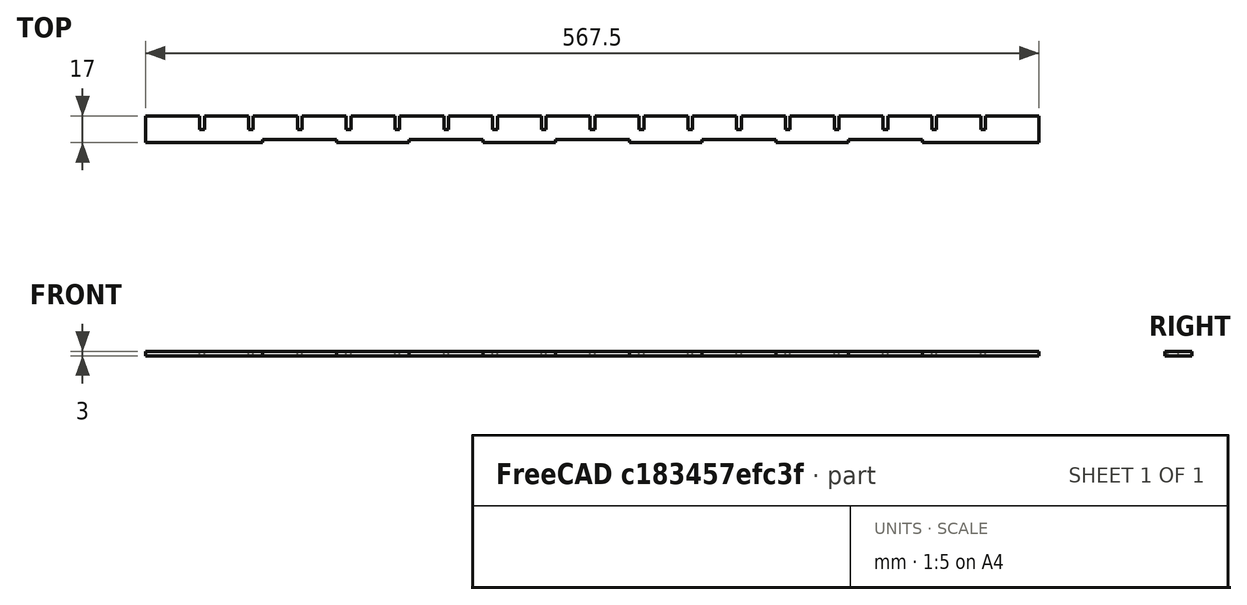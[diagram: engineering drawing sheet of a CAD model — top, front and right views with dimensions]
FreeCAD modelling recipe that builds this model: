
FCSTD DOCUMENT  (FreeCAD 0.16R6706 (Git))
Label: Leiste_lang_mitAufnahme_2x
License: All rights reserved
LicenseURL: http://de.wikipedia.org/wiki/Alle_Rechte_vorbehalten
objects: Sketcher::SketchObject×1, PartDesign::Pad×1
note: 3 computed .brp shape members not serialized (recipe doc carries the construction recipe); baked Part::Feature solids carry a one-line shape summary decoded from their .brp

FEATURE [Sketcher::SketchObject] Sketch
  sketch-geometry (97):
    g0: LineSegment StartX=0 StartY=0 StartZ=0 EndX=0 EndY=17 EndZ=0
    g1: LineSegment StartX=0 StartY=17 StartZ=0 EndX=34.5 EndY=17 EndZ=0
    g2: LineSegment StartX=34.5 StartY=17 StartZ=0 EndX=34.5 EndY=8.5 EndZ=0
    g3: LineSegment StartX=34.5 StartY=8.5 StartZ=0 EndX=37.5 EndY=8.5 EndZ=0
    g4: LineSegment StartX=37.5 StartY=8.5 StartZ=0 EndX=37.5 EndY=17 EndZ=0
    g5: LineSegment StartX=37.5 StartY=17 StartZ=0 EndX=65.5 EndY=17 EndZ=0
    g6: LineSegment StartX=65.5 StartY=17 StartZ=0 EndX=65.5 EndY=8.5 EndZ=0
    g7: LineSegment StartX=65.5 StartY=8.5 StartZ=0 EndX=68.5 EndY=8.5 EndZ=0
    g8: LineSegment StartX=68.5 StartY=8.5 StartZ=0 EndX=68.5 EndY=17 EndZ=0
    g9: LineSegment StartX=68.5 StartY=17 StartZ=0 EndX=96.5 EndY=17 EndZ=0
    g10: LineSegment StartX=96.5 StartY=17 StartZ=0 EndX=96.5 EndY=8.5 EndZ=0
    g11: LineSegment StartX=96.5 StartY=8.5 StartZ=0 EndX=99.5 EndY=8.5 EndZ=0
    g12: LineSegment StartX=99.5 StartY=8.5 StartZ=0 EndX=99.5 EndY=17 EndZ=0
    g13: LineSegment StartX=99.5 StartY=17 StartZ=0 EndX=127.5 EndY=17 EndZ=0
    g14: LineSegment StartX=127.5 StartY=17 StartZ=0 EndX=127.5 EndY=8.5 EndZ=0
    g15: LineSegment StartX=127.5 StartY=8.5 StartZ=0 EndX=130.5 EndY=8.5 EndZ=0
    g16: LineSegment StartX=130.5 StartY=8.5 StartZ=0 EndX=130.5 EndY=17 EndZ=0
    g17: LineSegment StartX=130.5 StartY=17 StartZ=0 EndX=158.5 EndY=17 EndZ=0
    g18: LineSegment StartX=158.5 StartY=17 StartZ=0 EndX=158.5 EndY=8.5 EndZ=0
    g19: LineSegment StartX=158.5 StartY=8.5 StartZ=0 EndX=161.5 EndY=8.5 EndZ=0
    g20: LineSegment StartX=161.5 StartY=8.5 StartZ=0 EndX=161.5 EndY=17 EndZ=0
    g21: LineSegment StartX=161.5 StartY=17 StartZ=0 EndX=189.5 EndY=17 EndZ=0
    g22: LineSegment StartX=189.5 StartY=17 StartZ=0 EndX=189.5 EndY=8.5 EndZ=0
    g23: LineSegment StartX=189.5 StartY=8.5 StartZ=0 EndX=192.5 EndY=8.5 EndZ=0
    g24: LineSegment StartX=192.5 StartY=8.5 StartZ=0 EndX=192.5 EndY=17 EndZ=0
    g25: LineSegment StartX=192.5 StartY=17 StartZ=0 EndX=220.5 EndY=17 EndZ=0
    g26: LineSegment StartX=220.5 StartY=17 StartZ=0 EndX=220.5 EndY=8.5 EndZ=0
    g27: LineSegment StartX=220.5 StartY=8.5 StartZ=0 EndX=223.5 EndY=8.5 EndZ=0
    g28: LineSegment StartX=223.5 StartY=8.5 StartZ=0 EndX=223.5 EndY=17 EndZ=0
    g29: LineSegment StartX=223.5 StartY=17 StartZ=0 EndX=251.5 EndY=17 EndZ=0
    g30: LineSegment StartX=251.5 StartY=17 StartZ=0 EndX=251.5 EndY=8.5 EndZ=0
    g31: LineSegment StartX=251.5 StartY=8.5 StartZ=0 EndX=254.5 EndY=8.5 EndZ=0
    g32: LineSegment StartX=254.5 StartY=8.5 StartZ=0 EndX=254.5 EndY=17 EndZ=0
    g33: LineSegment StartX=254.5 StartY=17 StartZ=0 EndX=282.5 EndY=17 EndZ=0
    g34: LineSegment StartX=282.5 StartY=17 StartZ=0 EndX=282.5 EndY=8.5 EndZ=0
    g35: LineSegment StartX=282.5 StartY=8.5 StartZ=0 EndX=285.5 EndY=8.5 EndZ=0
    g36: LineSegment StartX=285.5 StartY=8.5 StartZ=0 EndX=285.5 EndY=17 EndZ=0
    g37: LineSegment StartX=285.5 StartY=17 StartZ=0 EndX=313.5 EndY=17 EndZ=0
    g38: LineSegment StartX=313.5 StartY=17 StartZ=0 EndX=313.5 EndY=8.5 EndZ=0
    g39: LineSegment StartX=313.5 StartY=8.5 StartZ=0 EndX=316.5 EndY=8.5 EndZ=0
    g40: LineSegment StartX=316.5 StartY=8.5 StartZ=0 EndX=316.5 EndY=17 EndZ=0
    g41: LineSegment StartX=316.5 StartY=17 StartZ=0 EndX=344.5 EndY=17 EndZ=0
    g42: LineSegment StartX=344.5 StartY=17 StartZ=0 EndX=344.5 EndY=8.5 EndZ=0
    g43: LineSegment StartX=344.5 StartY=8.5 StartZ=0 EndX=347.5 EndY=8.5 EndZ=0
    g44: LineSegment StartX=347.5 StartY=8.5 StartZ=0 EndX=347.5 EndY=17 EndZ=0
    g45: LineSegment StartX=347.5 StartY=17 StartZ=0 EndX=375.5 EndY=17 EndZ=0
    g46: LineSegment StartX=375.5 StartY=17 StartZ=0 EndX=375.5 EndY=8.5 EndZ=0
    g47: LineSegment StartX=375.5 StartY=8.5 StartZ=0 EndX=378.5 EndY=8.5 EndZ=0
    g48: LineSegment StartX=378.5 StartY=8.5 StartZ=0 EndX=378.5 EndY=17 EndZ=0
    g49: LineSegment StartX=378.5 StartY=17 StartZ=0 EndX=406.5 EndY=17 EndZ=0
    g50: LineSegment StartX=406.5 StartY=17 StartZ=0 EndX=406.5 EndY=8.5 EndZ=0
    g51: LineSegment StartX=406.5 StartY=8.5 StartZ=0 EndX=409.5 EndY=8.5 EndZ=0
    g52: LineSegment StartX=409.5 StartY=8.5 StartZ=0 EndX=409.5 EndY=17 EndZ=0
    g53: LineSegment StartX=409.5 StartY=17 StartZ=0 EndX=437.5 EndY=17 EndZ=0
    g54: LineSegment StartX=437.5 StartY=17 StartZ=0 EndX=437.5 EndY=8.5 EndZ=0
    g55: LineSegment StartX=437.5 StartY=8.5 StartZ=0 EndX=440.5 EndY=8.5 EndZ=0
    g56: LineSegment StartX=440.5 StartY=8.5 StartZ=0 EndX=440.5 EndY=17 EndZ=0
    g57: LineSegment StartX=440.5 StartY=17 StartZ=0 EndX=468.5 EndY=17 EndZ=0
    g58: LineSegment StartX=468.5 StartY=17 StartZ=0 EndX=468.5 EndY=8.5 EndZ=0
    g59: LineSegment StartX=468.5 StartY=8.5 StartZ=0 EndX=471.5 EndY=8.5 EndZ=0
    g60: LineSegment StartX=471.5 StartY=8.5 StartZ=0 EndX=471.5 EndY=17 EndZ=0
    g61: LineSegment StartX=471.5 StartY=17 StartZ=0 EndX=499.5 EndY=17 EndZ=0
    g62: LineSegment StartX=499.5 StartY=17 StartZ=0 EndX=499.5 EndY=8.5 EndZ=0
    g63: LineSegment StartX=499.5 StartY=8.5 StartZ=0 EndX=502.5 EndY=8.5 EndZ=0
    g64: LineSegment StartX=502.5 StartY=8.5 StartZ=0 EndX=502.5 EndY=17 EndZ=0
    g65: LineSegment StartX=502.5 StartY=17 StartZ=0 EndX=530.5 EndY=17 EndZ=0
    g66: LineSegment StartX=530.5 StartY=17 StartZ=0 EndX=530.5 EndY=8.5 EndZ=0
    g67: LineSegment StartX=530.5 StartY=8.5 StartZ=0 EndX=533.5 EndY=8.5 EndZ=0
    g68: LineSegment StartX=533.5 StartY=8.5 StartZ=0 EndX=533.5 EndY=17 EndZ=0
    g69: LineSegment StartX=533.5 StartY=17 StartZ=0 EndX=567.5 EndY=17 EndZ=0
    g70: LineSegment StartX=567.5 StartY=17 StartZ=0 EndX=567.5 EndY=0 EndZ=0
    g71: LineSegment StartX=567.5 StartY=0 StartZ=0 EndX=493.5 EndY=0 EndZ=0
    g72: LineSegment StartX=121.5 StartY=0 StartZ=0 EndX=121.5 EndY=2 EndZ=0
    g73: LineSegment StartX=121.5 StartY=2 StartZ=0 EndX=74.5 EndY=2 EndZ=0
    g74: LineSegment StartX=74.5 StartY=2 StartZ=0 EndX=74.5 EndY=0 EndZ=0
    g75: LineSegment StartX=74.5 StartY=0 StartZ=0 EndX=0 EndY=0 EndZ=0
    g76: LineSegment StartX=214.5 StartY=0 StartZ=0 EndX=214.5 EndY=2 EndZ=0
    g77: LineSegment StartX=214.5 StartY=2 StartZ=0 EndX=167.5 EndY=2 EndZ=0
    g78: LineSegment StartX=167.5 StartY=2 StartZ=0 EndX=167.5 EndY=0 EndZ=0
    g79: LineSegment StartX=307.5 StartY=0 StartZ=0 EndX=307.5 EndY=2 EndZ=0
    g80: LineSegment StartX=307.5 StartY=2 StartZ=0 EndX=260.5 EndY=2 EndZ=0
    g81: LineSegment StartX=260.5 StartY=2 StartZ=0 EndX=260.5 EndY=0 EndZ=0
    g82: LineSegment StartX=400.5 StartY=0 StartZ=0 EndX=400.5 EndY=2 EndZ=0
    g83: LineSegment StartX=400.5 StartY=2 StartZ=0 EndX=353.5 EndY=2 EndZ=0
    g84: LineSegment StartX=353.5 StartY=2 StartZ=0 EndX=353.5 EndY=0 EndZ=0
    g85: LineSegment StartX=493.5 StartY=0 StartZ=0 EndX=493.5 EndY=2 EndZ=0
    g86: LineSegment StartX=493.5 StartY=2 StartZ=0 EndX=446.5 EndY=2 EndZ=0
    g87: LineSegment StartX=446.5 StartY=2 StartZ=0 EndX=446.5 EndY=0 EndZ=0
    g88: LineSegment StartX=446.5 StartY=0 StartZ=0 EndX=400.5 EndY=0 EndZ=0
    g89: LineSegment StartX=167.5 StartY=0 StartZ=0 EndX=121.5 EndY=0 EndZ=0
    g90: LineSegment StartX=260.5 StartY=0 StartZ=0 EndX=214.5 EndY=0 EndZ=0
    g91: LineSegment StartX=353.5 StartY=0 StartZ=0 EndX=307.5 EndY=0 EndZ=0
    g92: LineSegment [constr] StartX=98 StartY=8.5 StartZ=0 EndX=98 EndY=0 EndZ=0
    g93: LineSegment [constr] StartX=191 StartY=8.5 StartZ=0 EndX=191 EndY=0 EndZ=0
    g94: LineSegment [constr] StartX=284 StartY=8.5 StartZ=0 EndX=284 EndY=0 EndZ=0
    g95: LineSegment [constr] StartX=377 StartY=8.5 StartZ=0 EndX=377 EndY=0 EndZ=0
    g96: LineSegment [constr] StartX=470 StartY=8.5 StartZ=0 EndX=470 EndY=0 EndZ=0
  constraints (296):
    c: Coincident(g-1,g0)
    c: PointOnObject(g0,g-2)
    c: Coincident(g0,g1)
    c: Horizontal(g1)
    c: Coincident(g1,g2)
    c: Vertical(g2)
    c: Coincident(g2,g3)
    c: Horizontal(g3)
    c: Coincident(g3,g4)
    c: Vertical(g4)
    c: Coincident(g4,g5)
    c: Horizontal(g5)
    c: DistanceX(g2,g3) = 3
    c: DistanceX(g1,g5) = 31
    c: DistanceY(g2,g1) = 8.5
    c: Equal(g2,g4)
    c: Coincident(g5,g6)
    c: Vertical(g6)
    c: Coincident(g6,g7)
    c: Horizontal(g7)
    c: Coincident(g7,g8)
    c: Vertical(g8)
    c: Coincident(g8,g9)
    c: Horizontal(g9)
    c: Coincident(g9,g10)
    c: Vertical(g10)
    c: Coincident(g10,g11)
    c: Horizontal(g11)
    c: Coincident(g11,g12)
    c: Vertical(g12)
    c: Coincident(g12,g13)
    c: Horizontal(g13)
    c: Coincident(g13,g14)
    c: Vertical(g14)
    c: Coincident(g14,g15)
    c: Horizontal(g15)
    c: Coincident(g15,g16)
    c: Vertical(g16)
    c: Coincident(g16,g17)
    c: Horizontal(g17)
    c: Coincident(g17,g18)
    c: Vertical(g18)
    c: Coincident(g18,g19)
    c: Horizontal(g19)
    c: Coincident(g19,g20)
    c: Vertical(g20)
    c: Coincident(g20,g21)
    c: Horizontal(g21)
    c: Coincident(g21,g22)
    c: Vertical(g22)
    c: Coincident(g22,g23)
    c: Horizontal(g23)
    c: Coincident(g23,g24)
    c: Vertical(g24)
    c: Coincident(g24,g25)
    c: Horizontal(g25)
    c: Coincident(g25,g26)
    c: Vertical(g26)
    c: Coincident(g26,g27)
    c: Horizontal(g27)
    c: Coincident(g27,g28)
    c: Vertical(g28)
    c: Coincident(g28,g29)
    c: Horizontal(g29)
    c: Coincident(g29,g30)
    c: Vertical(g30)
    c: Coincident(g30,g31)
    c: Horizontal(g31)
    c: Coincident(g31,g32)
    c: Vertical(g32)
    c: Coincident(g32,g33)
    c: Horizontal(g33)
    c: Coincident(g33,g34)
    c: Vertical(g34)
    c: Coincident(g34,g35)
    c: Horizontal(g35)
    c: Coincident(g35,g36)
    c: Vertical(g36)
    c: Coincident(g36,g37)
    c: Horizontal(g37)
    c: Coincident(g37,g38)
    c: Vertical(g38)
    c: Coincident(g38,g39)
    c: Horizontal(g39)
    c: Coincident(g39,g40)
    c: Vertical(g40)
    c: Coincident(g40,g41)
    c: Horizontal(g41)
    c: Coincident(g41,g42)
    c: Vertical(g42)
    c: Coincident(g42,g43)
    c: Horizontal(g43)
    c: Coincident(g43,g44)
    c: Vertical(g44)
    c: Coincident(g44,g45)
    c: Horizontal(g45)
    c: Coincident(g45,g46)
    c: Vertical(g46)
    c: Coincident(g46,g47)
    c: Horizontal(g47)
    c: Coincident(g47,g48)
    c: Vertical(g48)
    c: Coincident(g48,g49)
    c: Horizontal(g49)
    c: Coincident(g49,g50)
    c: Vertical(g50)
    c: Coincident(g50,g51)
    c: Horizontal(g51)
    c: Coincident(g51,g52)
    c: Vertical(g52)
    c: Coincident(g52,g53)
    c: Horizontal(g53)
    c: Coincident(g53,g54)
    c: Vertical(g54)
    c: Coincident(g54,g55)
    c: Horizontal(g55)
    c: Coincident(g55,g56)
    c: Vertical(g56)
    c: Coincident(g56,g57)
    c: Horizontal(g57)
    c: Coincident(g57,g58)
    c: Vertical(g58)
    c: Coincident(g58,g59)
    c: Horizontal(g59)
    c: Coincident(g59,g60)
    c: Vertical(g60)
    c: Coincident(g60,g61)
    c: Horizontal(g61)
    c: Coincident(g61,g62)
    c: Vertical(g62)
    c: Coincident(g62,g63)
    c: Horizontal(g63)
    c: Coincident(g63,g64)
    c: Vertical(g64)
    c: Coincident(g64,g65)
    c: Horizontal(g65)
    c: Coincident(g65,g66)
    c: Vertical(g66)
    c: Coincident(g66,g67)
    c: Horizontal(g67)
    c: Coincident(g67,g68)
    c: Vertical(g68)
    c: Coincident(g68,g69)
    c: Horizontal(g69)
    c: Coincident(g69,g70)
    c: Vertical(g70)
    c: Coincident(g70,g71)
    c: Coincident(g75,g-1)
    c: Equal(g4,g6)
    c: Equal(g6,g8)
    c: Equal(g8,g10)
    c: Equal(g10,g12)
    c: Equal(g12,g14)
    c: Equal(g14,g16)
    c: Equal(g16,g18)
    c: Equal(g18,g20)
    c: Equal(g20,g22)
    c: Equal(g22,g24)
    c: Equal(g24,g26)
    c: Equal(g26,g28)
    c: Equal(g28,g30)
    c: Equal(g30,g32)
    c: Equal(g32,g34)
    c: Equal(g34,g36)
    c: Equal(g36,g38)
    c: Equal(g38,g40)
    c: Equal(g40,g42)
    c: Equal(g42,g44)
    c: Equal(g44,g46)
    c: Equal(g46,g48)
    c: Equal(g48,g50)
    c: Equal(g50,g52)
    c: Equal(g52,g54)
    c: Equal(g54,g56)
    c: Equal(g56,g58)
    c: Equal(g58,g60)
    c: Equal(g60,g62)
    c: Equal(g62,g64)
    c: Equal(g64,g66)
    c: Equal(g66,g68)
    c: Equal(g5,g9)
    c: Equal(g9,g13)
    c: Equal(g3,g7)
    c: Equal(g7,g11)
    c: DistanceX(g-1,g70) = 567.5
    c: Equal(g13,g17)
    c: Equal(g17,g21)
    c: Equal(g11,g15)
    c: Equal(g15,g19)
    c: Equal(g21,g25)
    c: Equal(g25,g29)
    c: Equal(g19,g23)
    c: Equal(g23,g27)
    c: Equal(g29,g33)
    c: Equal(g33,g37)
    c: Equal(g37,g41)
    c: Equal(g27,g31)
    c: Equal(g31,g35)
    c: Equal(g35,g39)
    c: Equal(g41,g45)
    c: Equal(g45,g49)
    c: Equal(g39,g43)
    c: Equal(g43,g47)
    c: Equal(g49,g53)
    c: Equal(g53,g57)
    c: Equal(g47,g51)
    c: Equal(g51,g55)
    c: Equal(g57,g61)
    c: Equal(g61,g65)
    c: Equal(g55,g59)
    c: Equal(g59,g63)
    c: Equal(g63,g67)
    c: DistanceY(g-1,g0) = 17
    c: DistanceX(g0,g1) = 34.5
    c: Coincident(g72,g73)
    c: Coincident(g73,g74)
    c: Horizontal(g73)
    c: Vertical(g72)
    c: Vertical(g74)
    c: PointOnObject(g74,g71)
    c: PointOnObject(g89,g72)
    c: PointOnObject(g75,g74)
    c: Tangent(g71,g75)
    c: DistanceY(g89,g72) = 2
    c: DistanceX(g74,g89) = 47
    c: Coincident(g76,g77)
    c: Coincident(g77,g78)
    c: Horizontal(g77)
    c: Vertical(g76)
    c: Vertical(g78)
    c: PointOnObject(g78,g71)
    c: Coincident(g79,g80)
    c: Coincident(g80,g81)
    c: Horizontal(g80)
    c: Vertical(g79)
    c: Vertical(g81)
    c: PointOnObject(g81,g71)
    c: Coincident(g82,g83)
    c: Coincident(g83,g84)
    c: Horizontal(g83)
    c: Vertical(g82)
    c: Vertical(g84)
    c: PointOnObject(g84,g71)
    c: Coincident(g85,g86)
    c: Coincident(g86,g87)
    c: Horizontal(g86)
    c: Vertical(g85)
    c: Vertical(g87)
    c: PointOnObject(g87,g71)
    c: PointOnObject(g71,g85)
    c: PointOnObject(g88,g87)
    c: Tangent(g71,g88)
    c: PointOnObject(g90,g76)
    c: PointOnObject(g89,g78)
    c: Tangent(g88,g89)
    c: PointOnObject(g91,g79)
    c: PointOnObject(g90,g81)
    c: Tangent(g88,g90)
    c: PointOnObject(g88,g82)
    c: PointOnObject(g91,g84)
    c: Tangent(g88,g91)
    c: Equal(g78,g81)
    c: Equal(g81,g84)
    c: Equal(g84,g87)
    c: Equal(g73,g77)
    c: Equal(g77,g80)
    c: Equal(g80,g83)
    c: Equal(g83,g86)
    c: Equal(g72,g78)
    c: Coincident(g72,g89)
    c: Coincident(g76,g90)
    c: Coincident(g79,g91)
    c: Coincident(g88,g82)
    c: Coincident(g85,g71)
    c: PointOnObject(g92,g11)
    c: PointOnObject(g92,g-1)
    c: Symmetric(g10,g11,g92)
    c: Symmetric(g74,g72,g92)
    c: PointOnObject(g93,g23)
    c: PointOnObject(g93,g-1)
    c: Symmetric(g22,g23,g93)
    c: Symmetric(g78,g76,g93)
    c: PointOnObject(g94,g35)
    c: PointOnObject(g94,g-1)
    c: Symmetric(g34,g35,g94)
    c: Symmetric(g81,g79,g94)
    c: PointOnObject(g95,g47)
    c: PointOnObject(g95,g-1)
    c: Vertical(g95)
    c: Symmetric(g46,g47,g95)
    c: Symmetric(g84,g82,g95)
    c: PointOnObject(g96,g59)
    c: PointOnObject(g96,g-1)
    c: Vertical(g96)
    c: Symmetric(g58,g59,g96)
    c: Symmetric(g87,g71,g96)
FEATURE [PartDesign::Pad] Pad
  Length = 3
  Length2 = 100
  Sketch = -> Sketch
  Type = 0
